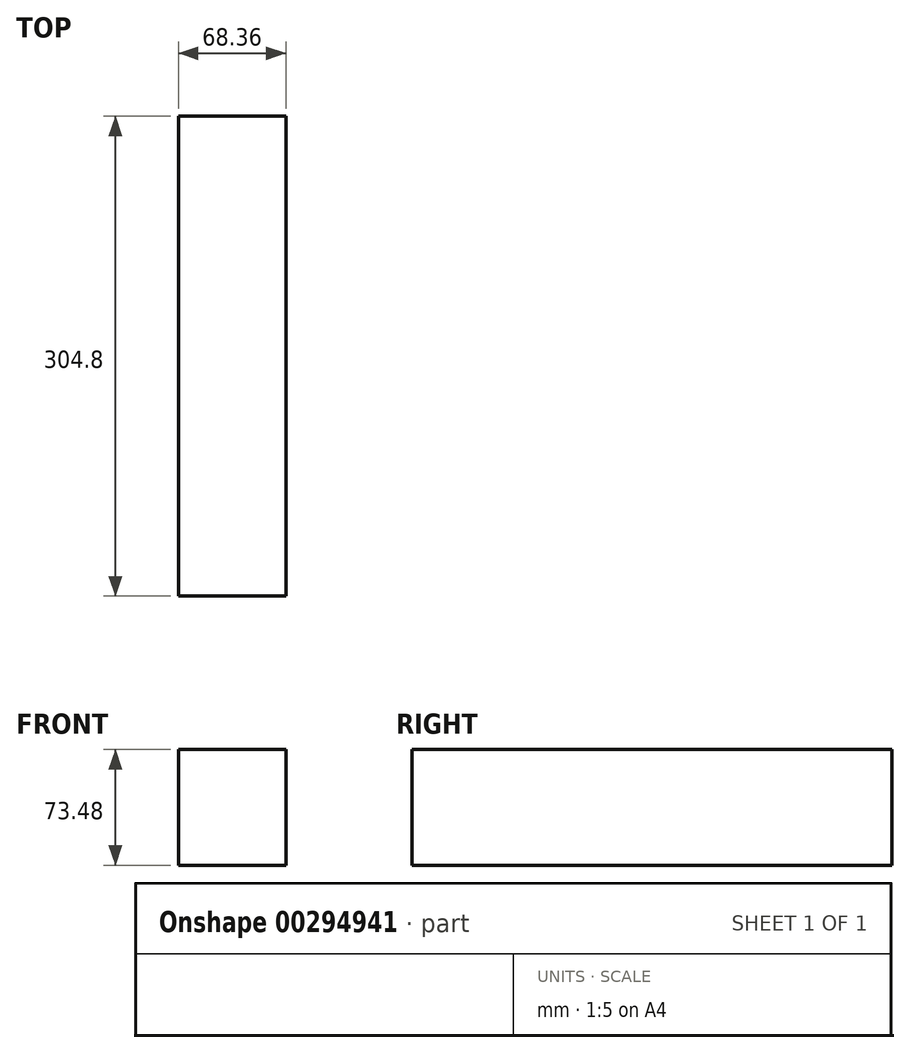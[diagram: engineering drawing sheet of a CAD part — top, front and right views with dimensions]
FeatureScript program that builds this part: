
annotation { "Feature Type Name" : "Feature", "Feature Type Description" : "" }
export const myFeature = defineFeature(function(context is Context, id is Id, definition is map)
    precondition{}
    {
        {
            var Q0;
            Q0=qCreatedBy(makeId("Front.planeOp"),FACE);
            var sketch = newSketch(context, id + "F0", { "sketchPlane" : qUnion([Q0])});
            skLineSegment(sketch, "E0.bottom", {"start": v(-58.35, 43.4) * mm, "end": v(10.01, 43.4) * mm});
            skLineSegment(sketch, "E0.top", {"start": v(-58.35, -30.08) * mm, "end": v(10.01, -30.08) * mm});
            skLineSegment(sketch, "E0.left", {"start": v(-58.35, 43.4) * mm, "end": v(-58.35, -30.08) * mm});
            skLineSegment(sketch, "E0.right", {"start": v(10.01, 43.4) * mm, "end": v(10.01, -30.08) * mm});
            skLineSegment(sketch, "E1.bottom", {"start": v(10.01, 26.93) * mm, "end": v(-41.09, 26.93) * mm});
            skLineSegment(sketch, "E1.top", {"start": v(10.01, -30.08) * mm, "end": v(-41.09, -30.08) * mm});
            skLineSegment(sketch, "E1.left", {"start": v(10.01, 26.93) * mm, "end": v(10.01, -30.08) * mm});
            skLineSegment(sketch, "E1.right", {"start": v(-41.09, 26.93) * mm, "end": v(-41.09, -30.08) * mm});
            skSolve(sketch);
        }
        {
            var Q0;
            Q0=makeQuery(id+"F0.imprint","IMPRINT",FACE,{"disambiguationData":[TD([[makeQuery(id+"F0.imprint","IMPRINT",EDGE,{"derivedFrom":sQuery(id+"F0.wireOp",EDGE,"E1.bottom")}),1.0]])]});
            var Q1;
            Q1=makeQuery(id+"F0.imprint","IMPRINT",FACE,{"disambiguationData":[TD([[makeQuery(id+"F0.imprint","IMPRINT",EDGE,{"derivedFrom":sQuery(id+"F0.wireOp",EDGE,"E0.bottom")}),-1.0]])]});
            extrude(context, id + "F1", {"entities" : qUnion([Q0, Q1]), "oppositeDirection" : true, "depth" : 304.8 * mm});
        }
        {
            var Q0;
            Q0=makeQuery(id+"F1.opExtrude","CAP_FACE",FACE,{"disambiguationData":[OSD([sQuery(id+"F0.wireOp",EDGE,"E0.bottom"),sQuery(id+"F0.wireOp",EDGE,"E0.top"),sQuery(id+"F0.wireOp",EDGE,"E0.left"),sQuery(id+"F0.wireOp",EDGE,"E0.right"),sQuery(id+"F0.wireOp",EDGE,"E1.top"),sQuery(id+"F0.wireOp",EDGE,"E1.left")])],"isStart":false});
            var sketch = newSketch(context, id + "F2", { "sketchPlane" : qUnion([Q0])});
            skLineSegment(sketch, "E2.bottom", {"start": v(21.04, 16.31) * mm, "end": v(44.4, 16.31) * mm});
            skLineSegment(sketch, "E2.top", {"start": v(21.04, -15.35) * mm, "end": v(44.4, -15.35) * mm});
            skLineSegment(sketch, "E2.left", {"start": v(21.04, 16.31) * mm, "end": v(21.04, -15.35) * mm});
            skLineSegment(sketch, "E2.right", {"start": v(44.4, 16.31) * mm, "end": v(44.4, -15.35) * mm});
            skSolve(sketch);
        }
        {
            var Q0;
            Q0=makeQuery(id+"F2.imprint","IMPRINT",FACE,{"disambiguationData":[TD([[makeQuery(id+"F2.imprint","IMPRINT",EDGE,{"derivedFrom":sQuery(id+"F2.wireOp",EDGE,"E2.bottom")}),-1.0]])]});
            extrude(context, id + "F3", {"entities" : qUnion([Q0]), "operationType" : NewBodyOperationType.ADD, "oppositeDirection" : true, "depth" : 152.4 * mm});
        }
    });
